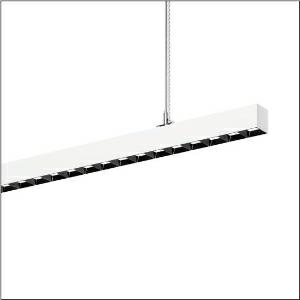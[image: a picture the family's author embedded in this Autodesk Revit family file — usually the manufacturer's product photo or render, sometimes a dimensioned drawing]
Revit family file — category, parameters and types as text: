
# Revit family: silica_r__21_51mx31tat7w_6f20
name_source: partatom
category: Lighting Fixtures
units: mm (PartAtom-declared; Revit-internal decimal feet)

## family parameters
Cut with Voids When Loaded = No
Host = Face
Light Source = No
Part Type = Normal
Room Calculation Point = No
Round Connector Dimension = Use Diameter
Shared = No

## types (1)
- --- (1 x LED, 6220 lm, 53.5 W, 6500K)
    Apparent Load = 54 VA
    CIE Flux Codes = 85 99 100 60 100
    Color Rendering = 80
    Color Temperature = 6500K
    Default Elevation = 1800 mm
    Description = Silica® 21, office luminaire, primary light control with darklight reflector, of PMMA, black, CAT 2 (L<= 3000cd/m²), light emission: direct/indirect distribution, primary light characteristic: symmetric, installation type: suspended mounting, LED, rated luminous flux: 6.220lm, luminous efficacy: 111lm/W, light colour: 8tw, colour temperature: 2700..6500K, control gear: ECG DALI, with terminal, 3+2-pole, max. 2.5mm², mains connection: 220..240V, AC, 50/60Hz, rated input power: 56.2W, luminaire housing, of aluminium, traffic white (RAL 9016), length: 1.204mm, width: 53mm, height: 53mm, protection rating (complete): IP20, insulation class (complete): insulation class I (protective earthing), certification: CE, permissible operating ambient temperature: 0..+35°C, standard: EN 50419, packaging unit: 1 piece
    Height = 53 mm
    Lamp = 1 x LED
    Lamp Light Flux = 6220 lm
    Lamp Power = 53.5 W
    Lamp count = 1
    Length = 1204 mm
    Luminous efficacy = 116 lm/W
    Manufacturer = Siteco
    ModVariant = No
    Model = 51MX31TAT7W
    Mounting Place = Ceiling
    Mounting Type = Pendant
    Number of Poles = 1
    OnlyDefault = Yes
    Power Factor = 1
    Product Name = Silica® 21
    Product group = office luminaire | ceiling pendant
    ProductGroupID = 905
    Protection Class = Protection class I
    Protection Degree = IP 20
    RLX_Detail_Level = 1
    RlxData = <blob elided: 40401 chars, md5=5d4fa8e5>
    Socket = socket
    Standby Power = 0 W
    System Light Flux = 6220 lm
    System Power = 54 W
    Type Comments = individual setting
    Type Image = l_1251637.jpg
    URL = http://relux.com
    VarID = @adj_045999
    Voltage = 0 V
    Weight = 0.00 kg
    Width = 53 mm

## geometry (parser evidence)
native form markers: Blend x4, Sweep x13
no freeform markers — native parametric forms only
